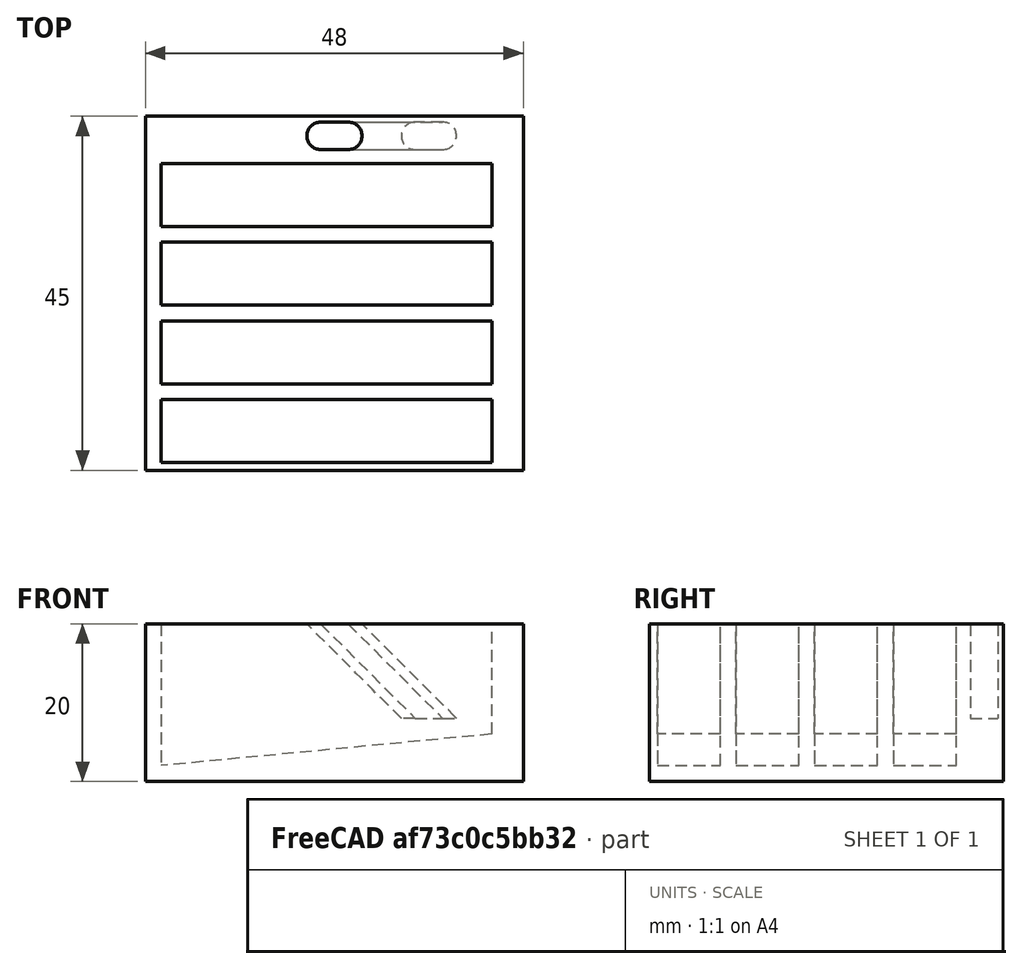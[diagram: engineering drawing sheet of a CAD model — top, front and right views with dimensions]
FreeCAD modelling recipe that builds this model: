
FCSTD DOCUMENT  (FreeCAD 1.2R20251230 (Git shallow))
Label: sloped_tray_insert_48x45x20
License: Creative Commons Attribution 4.0
LicenseURL: https://creativecommons.org/licenses/by/4.0/
objects: Part::Feature×6, Part::Cut×5, App::Point×1, Sketcher::SketchObject×1, PartDesign::Pad×1, PartDesign::Body×1
note: 17 computed .brp shape members not serialized (recipe doc carries the construction recipe); baked Part::Feature solids carry a one-line shape summary decoded from their .brp

FEATURE [App::Point] Origin001
  Role = Origin
FEATURE [Sketcher::SketchObject] Sketch_01_Base_48x45
  ArcFitTolerance = 1e-06
  ExternalTypes = [0]
  FullyConstrained = false
  MakeInternals = false
  sketch-geometry (4):
    g0: LineSegment StartX=0 StartY=0 StartZ=0 EndX=48 EndY=0 EndZ=0
    g1: LineSegment StartX=48 StartY=0 StartZ=0 EndX=48 EndY=45 EndZ=0
    g2: LineSegment StartX=48 StartY=45 StartZ=0 EndX=0 EndY=45 EndZ=0
    g3: LineSegment StartX=0 StartY=45 StartZ=0 EndX=0 EndY=0 EndZ=0
  constraints (4):
    c: Coincident(g0,g1)
    c: Coincident(g1,g2)
    c: Coincident(g2,g3)
    c: Coincident(g3,g0)
FEATURE [PartDesign::Pad] Pad_02_Base_Block_20
  Direction = (0,0,1)
  Length = 20
  Length2 = 10
  Profile = -> Sketch_01_Base_48x45
  Refine = true
  SideType = 0
  Suppressed = false
  Type = 0
  Type2 = 0
FEATURE [PartDesign::Body] Body_SlopedTrayInsert
  AllowCompound = true
  Group = -> [Sketch_01_Base_48x45,Pad_02_Base_Block_20]
  Origin = -> Origin
  Tip = -> Pad_02_Base_Block_20
FEATURE [Part::Feature] _03_Base_For_Sloped_Cuts
  shape: bbox 48 x 45 x 20 mm, 6 faces (baked)
FEATURE [Part::Feature] _04_Tool_Sloped_Recess_1_6to12mm
  shape: bbox 42 x 8 x 19 mm, 6 faces (baked)
FEATURE [Part::Cut] _05_Cut_Sloped_Recess_1
  Base = -> _03_Base_For_Sloped_Cuts
  Refine = true
  Tool = -> _04_Tool_Sloped_Recess_1_6to12mm
FEATURE [Part::Feature] _04_Tool_Sloped_Recess_2_6to12mm
  shape: bbox 42 x 8 x 19 mm, 6 faces (baked)
FEATURE [Part::Cut] _05_Cut_Sloped_Recess_2
  Base = -> _05_Cut_Sloped_Recess_1
  Refine = true
  Tool = -> _04_Tool_Sloped_Recess_2_6to12mm
FEATURE [Part::Feature] _04_Tool_Sloped_Recess_3_6to12mm
  shape: bbox 42 x 8 x 19 mm, 6 faces (baked)
FEATURE [Part::Cut] _05_Cut_Sloped_Recess_3
  Base = -> _05_Cut_Sloped_Recess_2
  Refine = true
  Tool = -> _04_Tool_Sloped_Recess_3_6to12mm
FEATURE [Part::Feature] _04_Tool_Sloped_Recess_4_6to12mm
  shape: bbox 42 x 8 x 19 mm, 6 faces (baked)
FEATURE [Part::Cut] _05_Cut_Sloped_Recess_4
  Base = -> _05_Cut_Sloped_Recess_3
  Refine = true
  Tool = -> _04_Tool_Sloped_Recess_4_6to12mm
FEATURE [Part::Feature] _06_Tool_Angled_3p5x7mm_Slot
  Placement = pos=(24,42.5,20) rot=(0,0,1;0rad)
  shape: bbox 19 x 3.5 x 12 mm, 6 faces (baked)
FEATURE [Part::Cut] _07_Cut_Angled_3p5x7mm_Slot  label="Final_SlopedTrayInsert_48x45x20"
  Base = -> _05_Cut_Sloped_Recess_4
  Refine = true
  Tool = -> _06_Tool_Angled_3p5x7mm_Slot
